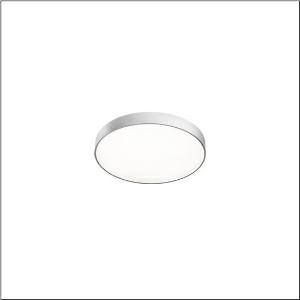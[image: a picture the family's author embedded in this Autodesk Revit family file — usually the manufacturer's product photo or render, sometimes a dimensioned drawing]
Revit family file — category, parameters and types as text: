
# Revit family: round_21_s_51mr34fd0321s
name_source: partatom
category: Lighting Fixtures
units: mm (PartAtom-declared; Revit-internal decimal feet)

## family parameters
Cut with Voids When Loaded = No
Host = Face
Light Source = No
Part Type = Normal
Room Calculation Point = No
Round Connector Dimension = Use Diameter
Shared = No

## types (1)
- Round 21 S (1 x LED, 3750 lm, 30.3 W, 3000K)
    Apparent Load = 30 VA
    CIE Flux Codes = 49 80 96 100 100
    Color Rendering = 80
    Color Temperature = 3000K
    Default Elevation = 1800 mm
    Description = Round 21 S, wall and ceiling luminaire, primary optical cover: cover, of PMMA, opal, light emission: direct distribution, primary light characteristic: symmetric, installation type: suspended mounting, surface-mounted, LED, rated luminous flux: 3.750lm, luminous efficacy: 124lm/W, light colour: 830, colour temperature: 3000K, with terminal, 5-pole, mains connection: 230V, AC, 50/60Hz, rated input power: 30.3W, housing, of aluminium, coated, silver, diameter: 400mm, height: 62mm, protection rating (complete): IP40, insulation class (complete): insulation class I (protective earthing), certification: CE, impact resistance: IK04, permissible operating ambient temperature: -10..+35°C, packaging unit: 1 piece
    Height = 87 mm
    Lamp = 1 x LED
    Lamp Light Flux = 3750 lm
    Lamp Power = 30.3 W
    Lamp count = 1
    Length = 400 mm
    Luminous efficacy = 124 lm/W
    Manufacturer = Siteco
    ModVariant = No
    Model = 51MR34FD0321S
    Mounting Place = Ceiling
    Mounting Type = Surface mounted
    Number of Poles = 1
    OnlyDefault = Yes
    Power Factor = 1
    Product Name = Round 21 S
    Product group = wall and ceiling luminaire
    ProductGroupID = 303
    Protection Class = Protection class I
    Protection Degree = IP 40
    RLX_Detail_Level = 1
    RLX_Emergency_Light_Flux = 0 lm
    RLX_Emergency_Type = 0
    RLX_Emergency_Type_DB = No
    RlxData = <blob elided: 11125 chars, md5=15155d71>
    Socket = socket
    Standby Power = 0 W
    System Light Flux = 3750 lm
    System Power = 30 W
    Type Comments = Product without accessories
    Type Image = l_1258309.jpg
    URL = http://relux.com
    VarID = ---
    Voltage = 0 V
    Weight = 0.00 kg
    Width = 0 mm  [stored 0 ft]

note: [stored X ft] marks values corroborated as IEEE doubles in the binary element streams (Revit-internal decimal feet)

## geometry (parser evidence)
native form markers: Sweep x8
no freeform markers — native parametric forms only
